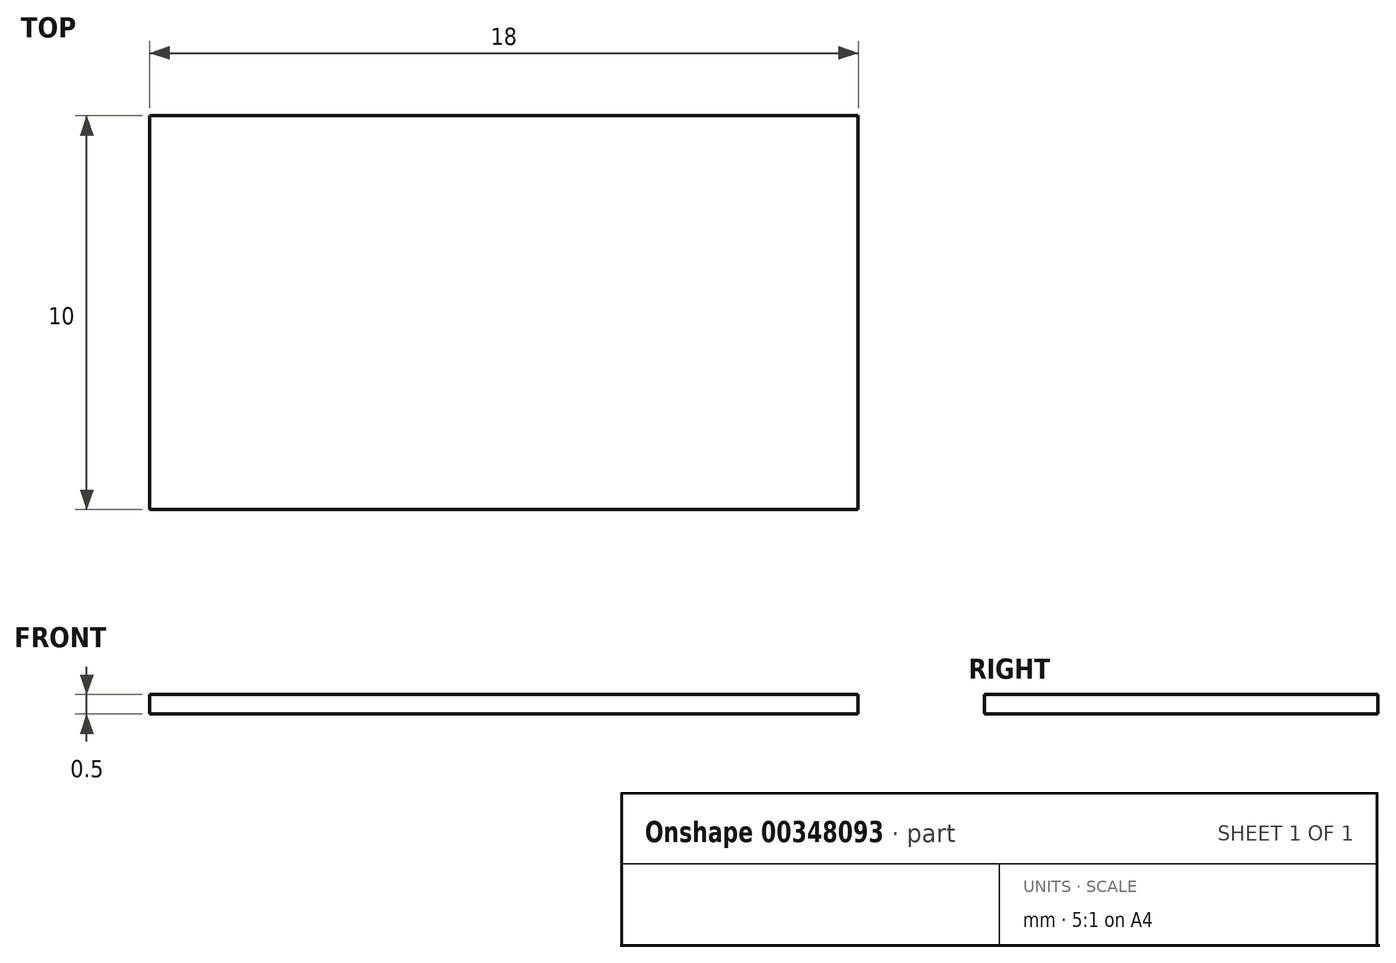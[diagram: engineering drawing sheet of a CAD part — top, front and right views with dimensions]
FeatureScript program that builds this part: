
annotation { "Feature Type Name" : "Feature", "Feature Type Description" : "" }
export const myFeature = defineFeature(function(context is Context, id is Id, definition is map)
    precondition{}
    {
        {
            var Q0;
            Q0=qCreatedBy(makeId("Front.planeOp"),FACE);
            var sketch = newSketch(context, id + "F0", { "sketchPlane" : qUnion([Q0])});
            skLineSegment(sketch, "E0.bottom", {"start": v(-31.5, 13.5) * mm, "end": v(-13.5, 13.5) * mm});
            skLineSegment(sketch, "E0.top", {"start": v(-31.5, 13) * mm, "end": v(-13.5, 13) * mm});
            skLineSegment(sketch, "E0.left", {"start": v(-31.5, 13.5) * mm, "end": v(-31.5, 13) * mm});
            skLineSegment(sketch, "E0.right", {"start": v(-13.5, 13.5) * mm, "end": v(-13.5, 13) * mm});
            skSolve(sketch);
        }
        {
            var Q0;
            Q0=makeQuery(id+"F0.imprint","IMPRINT",FACE,{"disambiguationData":[TD([[makeQuery(id+"F0.imprint","IMPRINT",EDGE,{"derivedFrom":sQuery(id+"F0.wireOp",EDGE,"E0.bottom")}),-1.0]])]});
            extrude(context, id + "F1", {"entities" : qUnion([Q0]), "depth" : 10 * mm});
        }
    });
